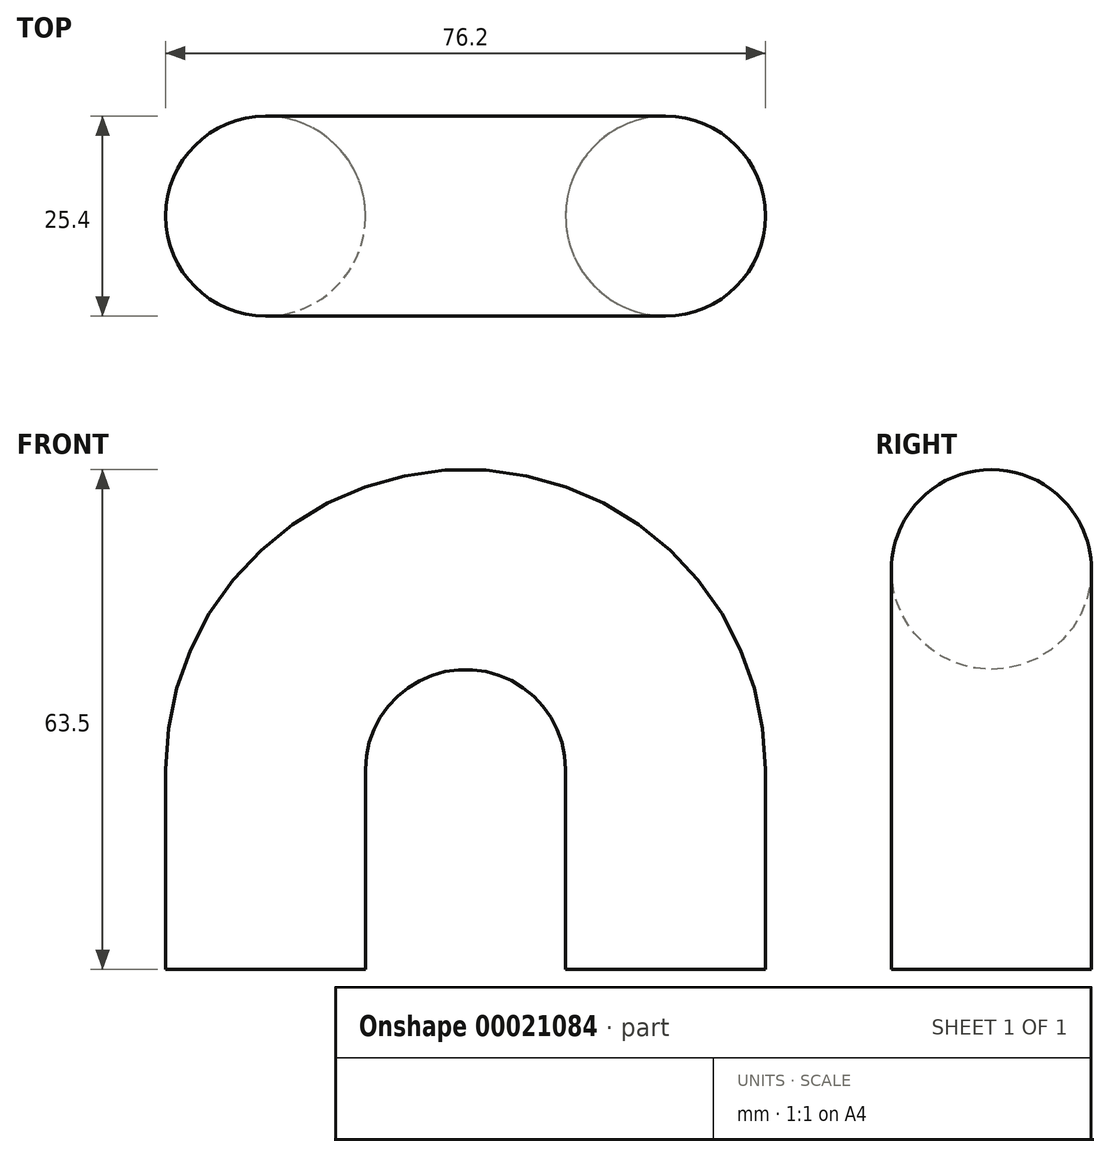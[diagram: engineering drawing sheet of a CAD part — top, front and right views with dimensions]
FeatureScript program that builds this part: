
annotation { "Feature Type Name" : "Feature", "Feature Type Description" : "" }
export const myFeature = defineFeature(function(context is Context, id is Id, definition is map)
    precondition{}
    {
        {
            var Q0;
            Q0=qCreatedBy(makeId("Front.planeOp"),FACE);
            var sketch = newSketch(context, id + "F0", { "sketchPlane" : qUnion([Q0])});
            skLineSegment(sketch, "E0", {"start": v(25.4, 0) * mm, "end": v(25.4, 25.4) * mm});
            skLineSegment(sketch, "E1", {"start": v(-25.4, 0) * mm, "end": v(-25.4, 25.4) * mm});
            skArc(sketch, "E2", {"start": v(-25.4, 25.4) * mm, "mid": v(0, 50.8) * mm, "end": v(25.4, 25.4) * mm});
            skSolve(sketch);
        }
        {
            var Q0;
            Q0=qCreatedBy(makeId("Top.planeOp"),FACE);
            var sketch = newSketch(context, id + "F1", { "sketchPlane" : qUnion([Q0])});
            skCircle(sketch, "E3", {"center": v(25.4, 0) * mm, "radius": 12.7 * mm});
            skSolve(sketch);
        }
        {
            var Q0;
            Q0=makeQuery(id+"F1.imprint","IMPRINT",FACE,{"disambiguationData":[TD([[makeQuery(id+"F1.imprint","IMPRINT",EDGE,{"derivedFrom":sQuery(id+"F1.wireOp",EDGE,"E3")}),1.0]])]});
            var Q1;
            Q1=sQuery(id+"F0.wireOp",EDGE,"E0");
            var Q2;
            Q2=sQuery(id+"F0.wireOp",EDGE,"E2");
            var Q3;
            Q3=sQuery(id+"F0.wireOp",EDGE,"E1");
            sweep(context, id + "F2", {"profiles" : qUnion([Q0]), "path" : qUnion([Q1, Q2, Q3])});
        }
    });
